# Revit family: Building-ConnessioniIEC309-GEWISS-67IB-PRESE-INTERBLOCCATE_IP67_SENZA_FONDO_MOD
name_source: partatom
category: Apparecchi elettrici
units: mm (PartAtom-declared; Revit-internal decimal feet)

## family parameters
Condiviso = Sì
Host = Superficie
Mantenere orientamento annotazione = Sì
Punto di calcolo locali = Sì
Quota connettore circolare = Usa diametro
Taglio con vuoti quando caricato = Sì
Tipo di parte = Normale

## types (18) — shared parameters
Catalogo = BUILDING
Catalogo Serie = 67 IB
Codice Electrocod = 2222
Con fondo = No
Corpo presa = GEWISS -BLU
Frequenza = 50/60 Hz
Frequenza nominale (Hz) = 50/60 Hz
Glow Wire Test = 850 °C
Glow wire test: = 850 °C
Grado di protezione = IP67
IDF = 3d99d921-5ba7-457f-9151-77f6686a7810
IDT = a7f1347e-7fe6-401d-a8af-d935eaffb75e
Immagine tipo = A.jpg
Interruttore = MT 6 kA Curva C
Produttore = GEWISS S.p.A.
Prospetto di default = 1219 mm
Protezione = Magnetotermico
Resistenza agli urti = IK08
SEO = Presa
Scheda Tecnica = https://www.gewiss.com
Simbolo presa = PRESAINDSTAGNA : 3P
Struttura = Grigio RAL - 7035
Temperatura di funzionamento = -25 ÷ +40 °C
Temperatura di utilizzo = -25 +40 °C
Termopressione con biglia = 125 °C
Tipologia = Verticale
URL = https://www.gewiss.com
Versione file RFA = 21.4
presa = rosso
zero-valued in all types: giallo

## per-type parameters (varying)
| type | Codice EAN | Colore | Colore: | Corrente nominale (A) | Corrente nominale (In) | Descrizione | Modello | N. poli | Numero di poli | Riferimento h | Tensione nominale | Tensione nominale: |
| GW66166N - PR.BL IP67 S.F.3P+T 32A 230V 9H MT60C | 8011564741096 | Blu | Blu | 32 | 32 | PR.BL IP67 S.F.3P+T 32A 230V 9H MT60C | GW66166N | 3P+T | 3P+N+T | 9 | 200 - 250 V | 200 - 250 V |
| GW66163N - PR.BL IP67 S.F.3P+T 32A 110V 4H MT60C | 8011564741065 | Giallo | Giallo | 32 | 32 | PR.BL IP67 S.F.3P+T 32A 110V 4H MT60C | GW66163N | 3P+T | 3P+N+T | 4 | 100 - 130 V | 100 - 130 V |
| GW66155N - PR.BL IP67 S.F.3P+T 16A 230V 9H MT60C | 8011564741003 | Blu | Blu | 16 | 16 | PR.BL IP67 S.F.3P+T 16A 230V 9H MT60C | GW66155N | 3P+T | 3P+T | 9 | 200 - 250 V | 200 - 250 V |
| GW66151N - PR.BL IP67 S.F.2P+T 16A 110V 4H MT60C | 8011564740969 | Giallo | Giallo | 16 | 16 | PR.BL IP67 S.F.2P+T 16A 110V 4H MT60C | GW66151N | 2P+T | 2P+T | 4 | 100 - 130 V | 100 - 130 V |
| GW66168N - PR.BL IP67 S.F.2P+T 32A 400V 9H MT60C | 8011564741119 | Rosso | Rosso | 32 | 32 | PR.BL IP67 S.F.2P+T 32A 400V 9H MT60C | GW66168N | 2P+T | 3P+T | 9 | 380 - 415 V | 380 - 415 V |
| GW66164N - PR.BL IP67 S.F.3P+N+T 32A 110V 4H MT60C | 8011564741072 | Giallo | Giallo | 32 | 32 | PR.BL IP67 S.F.3P+N+T 32A 110V 4H MT60C | GW66164N | 3P+N+T | 2P+T | 4 | 100 - 130 V | 100 - 130 V |
| GW66153N - PR.BL IP67 S.F.3P+N+T 16A 110V 4H MT60C | 8011564740983 | Giallo | Giallo | 16 | 16 | PR.BL IP67 S.F.3P+N+T 16A 110V 4H MT60C | GW66153N | 3P+N+T | 3P+N+T | 4 | 100 - 130 V | 100 - 130 V |
| GW66158N - PR.BL IP67 S.F.3P+T 16A 400V 6H MT60C | 8011564741034 | Rosso | Rosso | 16 | 16 | PR.BL IP67 S.F.3P+T 16A 400V 6H MT60C | GW66158N | 3P+T | 3P+T | 6 | 380 - 415 V | 380 - 415 V |
| GW66152N - PR.BL IP67 S.F.3P+T 16A 110V 4H MT60C | 8011564740976 | Giallo | Giallo | 16 | 16 | PR.BL IP67 S.F.3P+T 16A 110V 4H MT60C | GW66152N | 3P+T | 3P+T | 4 | 100 - 130 V | 100 - 130 V |
| GW66169N - PR.BL IP67 S.F.3P+T 32A 400V 6H MT60C | 8011564741126 | Rosso | Rosso | 32 | 32 | PR.BL IP67 S.F.3P+T 32A 400V 6H MT60C | GW66169N | 3P+T | 3P+N+T | 6 | 380 - 415 V | 380 - 415 V |
| GW66167N - PR.BL IP67 S.F.3P+N+T 32A 230V 9H MT60C | 8011564741102 | Blu | Blu | 32 | 32 | PR.BL IP67 S.F.3P+N+T 32A 230V 9H MT60C | GW66167N | 3P+N+T | 2P+T | 9 | 200 - 250 V | 200 - 250 V |
| GW66170N - PR.BL IP67 S.F.3P+N+T 32A 400V 6H MT60C | 8011564741133 | Rosso | Rosso | 32 | 32 | PR.BL IP67 S.F.3P+N+T 32A 400V 6H MT60C | GW66170N | 3P+N+T | 2P+T | 6 | 380 - 415 V | 380 - 415 V |
| GW66156N - PR.BL IP67 S.F.3P+N+T 16A 230V 9H MT60C | 8011564741010 | Blu | Blu | 16 | 16 | PR.BL IP67 S.F.3P+N+T 16A 230V 9H MT60C | GW66156N | 3P+N+T | 3P+N+T | 9 | 200 - 250 V | 200 - 250 V |
| GW66165N - PR.BL IP67 S.F.2P+T 32A 230V 6H MT60C | 8011564741089 | Blu | Blu | 32 | 32 | PR.BL IP67 S.F.2P+T 32A 230V 6H MT60C | GW66165N | 2P+T | 3P+T | 6 | 200 - 250 V | 200 - 250 V |
| GW66162N - PR.BL IP67 S.F.2P+T 32A 110V 4H MT60C | 8011564741058 | Giallo | Giallo | 32 | 32 | PR.BL IP67 S.F.2P+T 32A 110V 4H MT60C | GW66162N | 2P+T | 3P+T | 4 | 100 - 130 V | 100 - 130 V |
| GW66157N - PR.BL IP67 S.F.2P+T 16A 400V 9H MT60C | 8011564741027 | Rosso | Rosso | 16 | 16 | PR.BL IP67 S.F.2P+T 16A 400V 9H MT60C | GW66157N | 2P+T | 2P+T | 9 | 380 - 415 V | 380 - 415 V |
| GW66154N - PR.BL IP67 S.F.2P+T 16A 230V 6H MT60C | 8011564740990 | Blu | Blu | 16 | 16 | PR.BL IP67 S.F.2P+T 16A 230V 6H MT60C | GW66154N | 2P+T | 2P+T | 6 | 200 - 250 V | 200 - 250 V |
| GW66159N - PR.BL IP67 S.F.3P+N+T 16A 400V 6H MT60C | 8011564741041 | Rosso | Rosso | 16 | 16 | PR.BL IP67 S.F.3P+N+T 16A 400V 6H MT60C | GW66159N | 3P+N+T | 3P+N+T | 6 | 380 - 415 V | 380 - 415 V |

## geometry (parser evidence)
native form markers: Sweep x4
no freeform markers — native parametric forms only
